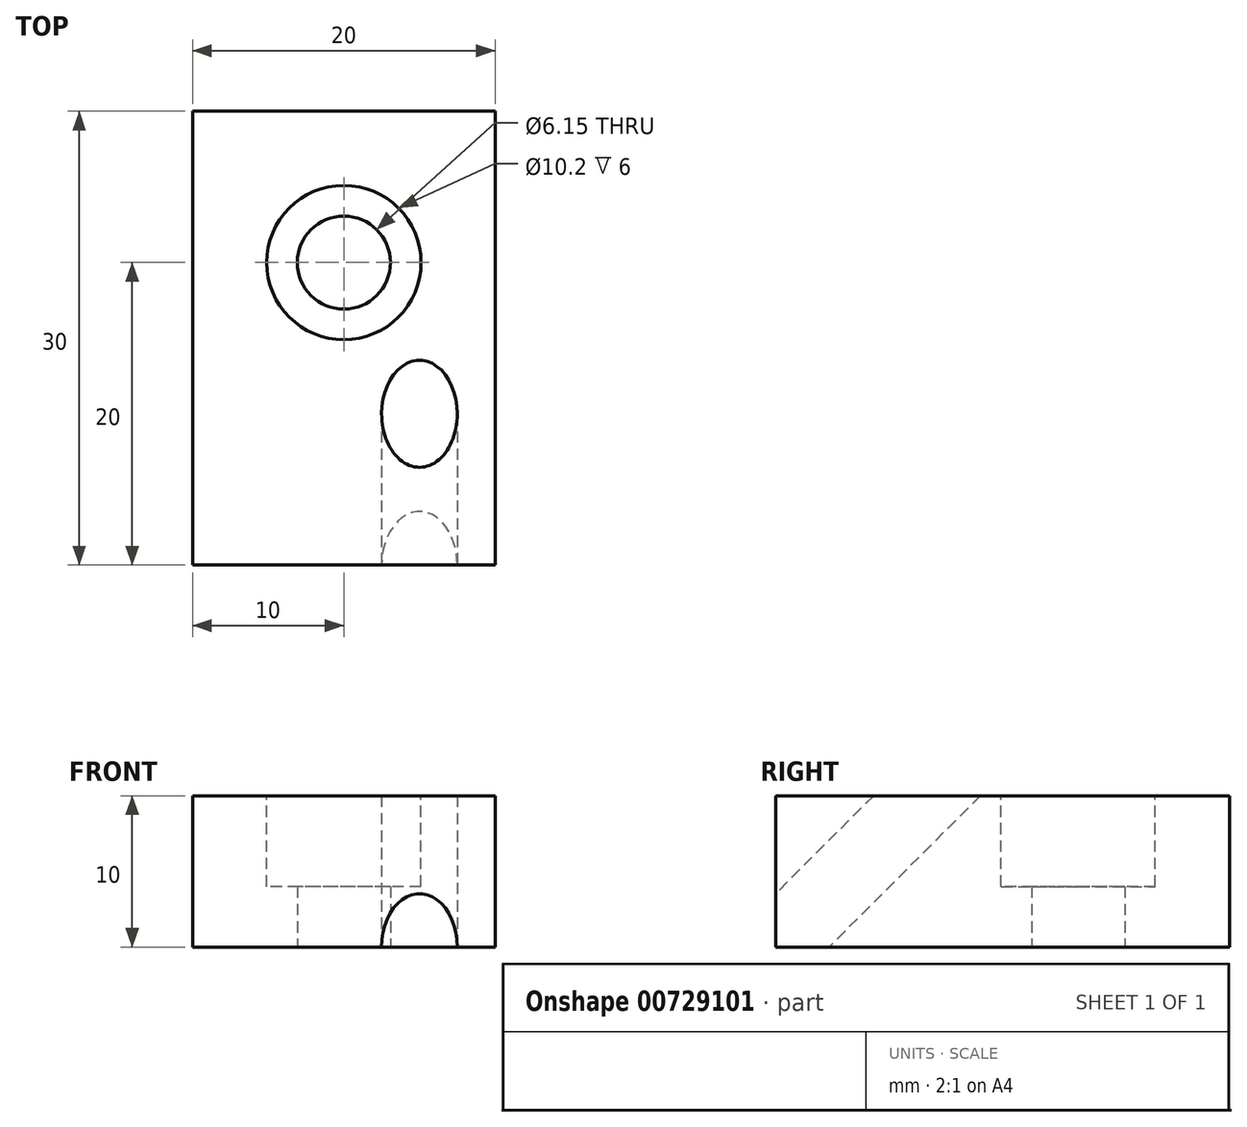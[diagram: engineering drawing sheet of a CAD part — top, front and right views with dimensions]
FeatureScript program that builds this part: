
annotation { "Feature Type Name" : "Feature", "Feature Type Description" : "" }
export const myFeature = defineFeature(function(context is Context, id is Id, definition is map)
    precondition{}
    {
        {
            var Q0;
            Q0=qCreatedBy(makeId("Top.planeOp"),FACE);
            var sketch = newSketch(context, id + "F0", { "sketchPlane" : qUnion([Q0])});
            skLineSegment(sketch, "E0.bottom", {"start": v(-10, 10) * mm, "end": v(10, 10) * mm});
            skLineSegment(sketch, "E0.top", {"start": v(-10, -20) * mm, "end": v(10, -20) * mm});
            skLineSegment(sketch, "E0.left", {"start": v(-10, 10) * mm, "end": v(-10, -20) * mm});
            skLineSegment(sketch, "E0.right", {"start": v(10, 10) * mm, "end": v(10, -20) * mm});
            skCircle(sketch, "E1", {"center": v(0, 0) * mm, "radius": 3.07 * mm});
            skPoint(sketch, "E2", {"position": v(0, 10) * mm});
            skSolve(sketch);
        }
        {
            var Q0;
            Q0=makeQuery(id+"F0.imprint","IMPRINT",FACE,{"disambiguationData":[TD([[makeQuery(id+"F0.imprint","IMPRINT",EDGE,{"derivedFrom":sQuery(id+"F0.wireOp",EDGE,"E0.bottom")}),-1.0]])]});
            extrude(context, id + "F1", {"entities" : qUnion([Q0]), "depth" : 10 * mm, "offsetDistance" : 25 * mm});
        }
        {
            var Q0;
            Q0=makeQuery(id+"F1.opExtrude","CAP_FACE",FACE,{"disambiguationData":[OSD([sQuery(id+"F0.wireOp",EDGE,"E0.bottom"),sQuery(id+"F0.wireOp",EDGE,"E0.top"),sQuery(id+"F0.wireOp",EDGE,"E0.left"),sQuery(id+"F0.wireOp",EDGE,"E0.right"),sQuery(id+"F0.wireOp",EDGE,"E1")])],"isStart":false});
            var sketch = newSketch(context, id + "F2", { "sketchPlane" : qUnion([Q0])});
            skCircle(sketch, "E3", {"center": v(0, 0) * mm, "radius": 5.1 * mm});
            skSolve(sketch);
        }
        {
            var Q0;
            Q0=makeQuery(id+"F2.imprint","IMPRINT",FACE,{"disambiguationData":[TD([[makeQuery(id+"F2.imprint","IMPRINT",EDGE,{"derivedFrom":sQuery(id+"F2.wireOp",EDGE,"E3")}),1.0]])]});
            extrude(context, id + "F3", {"entities" : qUnion([Q0]), "operationType" : NewBodyOperationType.REMOVE, "oppositeDirection" : true, "depth" : 6 * mm, "offsetDistance" : 25 * mm});
        }
        {
            var Q0;
            Q0=makeQuery(id+"F1.opExtrude","CAP_EDGE",EDGE,{"disambiguationData":[OSD([sQuery(id+"F0.wireOp",EDGE,"E0.top")])],"isStart":true});
            cPlane(context, id + "F4", {"entities" : qUnion([Q0]), "cplaneType" : CPlaneType.LINE_ANGLE, "offset" : 25 * mm, "angle" : 45 * degree, "width" : 150 * mm, "height" : 150 * mm});
        }
        {
            var Q0;
            Q0=qCreatedBy(id+"F4.planeOp",FACE);
            var sketch = newSketch(context, id + "F5", { "sketchPlane" : qUnion([Q0])});
            skCircle(sketch, "E4", {"center": v(-5, 14.14) * mm, "radius": 2.5 * mm});
            skSolve(sketch);
        }
        {
            var Q0;
            Q0=makeQuery(id+"F5.imprint","IMPRINT",FACE,{"disambiguationData":[TD([[makeQuery(id+"F5.imprint","IMPRINT",EDGE,{"derivedFrom":sQuery(id+"F5.wireOp",EDGE,"E4")}),1.0]])]});
            extrude(context, id + "F6", {"entities" : qUnion([Q0]), "operationType" : NewBodyOperationType.REMOVE, "depth" : 25 * mm, "offsetDistance" : 25 * mm});
        }
    });
